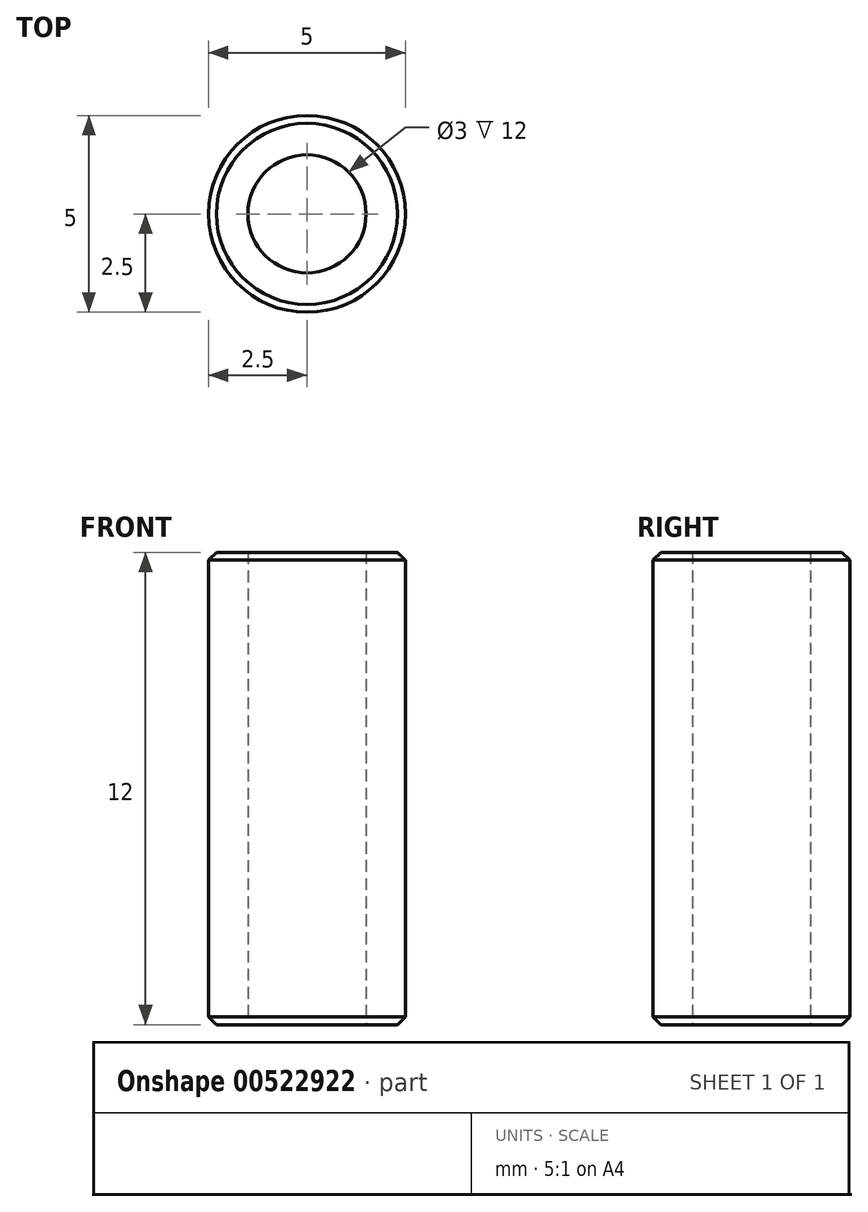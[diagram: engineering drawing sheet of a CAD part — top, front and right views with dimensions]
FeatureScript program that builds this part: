
annotation { "Feature Type Name" : "Feature", "Feature Type Description" : "" }
export const myFeature = defineFeature(function(context is Context, id is Id, definition is map)
    precondition{}
    {
        {
            var Q0;
            Q0=qCreatedBy(makeId("Top.planeOp"),FACE);
            var sketch = newSketch(context, id + "F0", { "sketchPlane" : qUnion([Q0])});
            skCircle(sketch, "E0", {"center": v(0, 0) * mm, "radius": 2.5 * mm});
            skSolve(sketch);
        }
        {
            var Q0;
            Q0=qSketchRegion(id+"F0",true);
            extrude(context, id + "F1", {"entities" : qUnion([Q0]), "depth" : 12 * mm});
        }
        {
            var Q0;
            Q0=makeQuery(id+"F1.opExtrude","CAP_FACE",FACE,{"disambiguationData":[OSD([sQuery(id+"F0.wireOp",EDGE,"E0")])],"isStart":false});
            var Q1;
            Q1=makeQuery(id+"F1.opExtrude","CAP_FACE",FACE,{"disambiguationData":[OSD([sQuery(id+"F0.wireOp",EDGE,"E0")])],"isStart":true});
            chamfer(context, id + "F2", {"entities" : qUnion([Q0, Q1]), "width" : 0.2 * mm, "tangentPropagation" : true});
        }
        {
            var Q0;
            Q0=sQuery(id+"F0.wireOp",VERTEX,"E0.center");
            var Q1;
            Q1=makeQuery(id+"F1.opExtrude","SWEPT_BODY",BODY,{"disambiguationData":[OSD([sQuery(id+"F0.wireOp",EDGE,"E0")])]});
            hole(context, id + "F3", {"style" : HoleStyle.SIMPLE, "endStyle" : HoleEndStyle.THROUGH, "oppositeDirection" : true, "holeDiameter" : 3 * mm, "isTappedThrough" : true, "tappedDepth" : 12 * mm, "tapClearance" : 3, "startFromSketch" : true, "locations" : qUnion([Q0]), "scope" : qUnion([Q1])});
        }
    });
